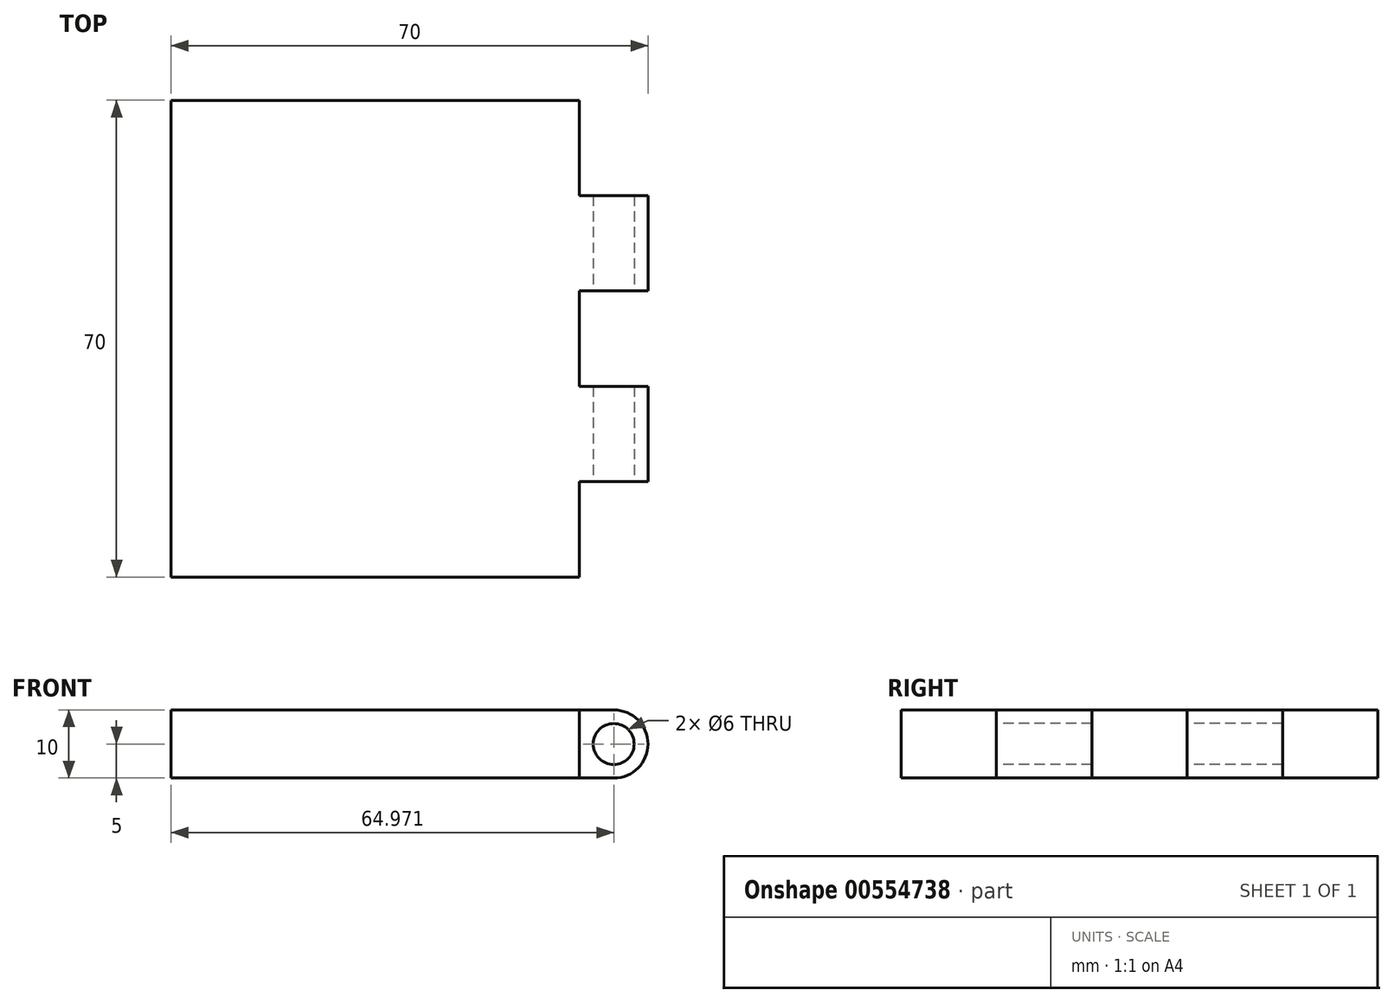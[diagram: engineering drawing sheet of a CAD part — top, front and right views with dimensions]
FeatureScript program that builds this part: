
annotation { "Feature Type Name" : "Feature", "Feature Type Description" : "" }
export const myFeature = defineFeature(function(context is Context, id is Id, definition is map)
    precondition{}
    {
        {
            var Q0;
            Q0=qCreatedBy(makeId("Top.planeOp"),FACE);
            var sketch = newSketch(context, id + "F0", { "sketchPlane" : qUnion([Q0])});
            skPoint(sketch, "E0.middle", {"position": v(0.02, 0.14) * mm});
            skLineSegment(sketch, "E1.0", {"start": v(24.97, 35.14) * mm, "end": v(-34.98, 35.14) * mm});
            skLineSegment(sketch, "E1.1", {"start": v(35.02, 21.14) * mm, "end": v(35.02, 7.14) * mm});
            skLineSegment(sketch, "E1.2", {"start": v(24.97, -34.86) * mm, "end": v(-34.98, -34.86) * mm});
            skLineSegment(sketch, "E1.3", {"start": v(-34.98, 35.14) * mm, "end": v(-34.98, -34.86) * mm});
            skLineSegment(sketch, "E2", {"start": v(25.02, -20.86) * mm, "end": v(35.02, -20.86) * mm});
            skLineSegment(sketch, "E3", {"start": v(25.02, -6.86) * mm, "end": v(35.02, -6.86) * mm});
            skLineSegment(sketch, "E4", {"start": v(25.02, 7.14) * mm, "end": v(35.02, 7.14) * mm});
            skLineSegment(sketch, "E5", {"start": v(25.02, 21.14) * mm, "end": v(35.02, 21.14) * mm});
            skPoint(sketch, "E6.orphan", {"position": v(25.02, -34.86) * mm});
            skLineSegment(sketch, "E7.trimOffspring", {"start": v(35.02, -6.86) * mm, "end": v(35.02, -20.86) * mm});
            skPoint(sketch, "E0.right.end.orphan", {"position": v(-24.98, -24.86) * mm});
            skPoint(sketch, "E0.bottom.end.orphan", {"position": v(-24.98, 25.14) * mm});
            skLineSegment(sketch, "E8", {"start": v(25.02, -20.86) * mm, "end": v(24.97, -20.86) * mm});
            skLineSegment(sketch, "E9", {"start": v(24.97, -20.86) * mm, "end": v(24.97, -34.86) * mm});
            skLineSegment(sketch, "E10", {"start": v(24.97, -6.86) * mm, "end": v(24.97, 35.14) * mm});
            skLineSegment(sketch, "E11", {"start": v(25.02, 21.14) * mm, "end": v(24.97, 21.14) * mm});
            skPoint(sketch, "E12.end.orphan", {"position": v(25.02, 35.14) * mm});
            skPoint(sketch, "E12.start.orphan", {"position": v(25.02, 25.14) * mm});
            skLineSegment(sketch, "E13", {"start": v(25.02, 7.14) * mm, "end": v(24.97, 7.14) * mm});
            skLineSegment(sketch, "E14", {"start": v(25.02, -6.86) * mm, "end": v(24.97, -6.86) * mm});
            skPoint(sketch, "E15.start.orphan", {"position": v(25.02, -24.86) * mm});
            skLineSegment(sketch, "E16.trimOffspring", {"start": v(25.02, -6.86) * mm, "end": v(25.02, -20.86) * mm});
            skSolve(sketch);
        }
        {
            var Q0;
            Q0=makeQuery(id+"F0.imprint","IMPRINT",FACE,{"disambiguationData":[TD([[makeQuery(id+"F0.imprint","IMPRINT",EDGE,{"derivedFrom":sQuery(id+"F0.wireOp",EDGE,"E0.bottom")}),-1.0]])]});
            var Q1;
            {var subQ3=sQuery(id+"F0.wireOp",EDGE,"E0.bottom");Q1=makeQuery(id+"F0.imprint","IMPRINT",FACE,{"disambiguationData":[TD([[makeQuery(id+"F0.imprint","IMPRINT",EDGE,{"derivedFrom":subQ3}),1.0]])]});}
            var Q2;
            {var subQ0=sQuery(id+"F0.wireOp",EDGE,"E2");Q2=makeQuery(id+"F0.imprint","IMPRINT",FACE,{"disambiguationData":[TD([[makeQuery(id+"F0.imprint","IMPRINT",EDGE,{"derivedFrom":subQ0}),1.0]])]});}
            var Q3;
            Q3=makeQuery(id+"F0.imprint","IMPRINT",FACE,{"disambiguationData":[TD([[makeQuery(id+"F0.imprint","IMPRINT",EDGE,{"derivedFrom":sQuery(id+"F0.wireOp",EDGE,"E1.1")}),-1.0]])]});
            var Q4;
            {var subQ1=sQuery(id+"F0.wireOp",EDGE,"E1.0");Q4=makeQuery(id+"F0.imprint","IMPRINT",FACE,{"disambiguationData":[TD([[makeQuery(id+"F0.imprint","IMPRINT",EDGE,{"derivedFrom":subQ1}),1.0]])]});}
            extrude(context, id + "F1", {"entities" : qUnion([Q0, Q1, Q2, Q3, Q4]), "depth" : 10 * mm, "offsetDistance" : 25 * mm});
        }
        {
            var Q0;
            Q0=makeQuery(id+"F1.opExtrude","SWEPT_FACE",FACE,{"disambiguationData":[OSD([sQuery(id+"F0.wireOp",EDGE,"E2")])]});
            var sketch = newSketch(context, id + "F2", { "sketchPlane" : qUnion([Q0])});
            skCircle(sketch, "E17", {"center": v(30, 5) * mm, "radius": 3 * mm});
            skPoint(sketch, "E17.centerSnap0", {"position": v(30, 10) * mm});
            skPoint(sketch, "E17.centerSnap1", {"position": v(35.02, 5) * mm});
            skArc(sketch, "E18", {"start": v(35.02, 5) * mm, "mid": v(33.54, 8.54) * mm, "end": v(30, 10) * mm});
            skArc(sketch, "E19", {"start": v(30, 0) * mm, "mid": v(33.54, 1.46) * mm, "end": v(35.02, 5) * mm});
            skSolve(sketch);
        }
        {
            var Q0;
            Q0=makeQuery(id+"F2.imprint","IMPRINT",FACE,{"disambiguationData":[TD([[makeQuery(id+"F2.imprint","IMPRINT",EDGE,{"derivedFrom":sQuery(id+"F2.wireOp",EDGE,"E17")}),1.0]])]});
            var Q1;
            {var subQ0=sQuery(id+"F2.wireOp",EDGE,"E18");Q1=makeQuery(id+"F2.imprint","IMPRINT",FACE,{"disambiguationData":[TD([[makeQuery(id+"F2.imprint","IMPRINT",EDGE,{"derivedFrom":subQ0}),-1.0]])]});}
            var Q2;
            {var subQ0=sQuery(id+"F2.wireOp",EDGE,"E19");Q2=makeQuery(id+"F2.imprint","IMPRINT",FACE,{"disambiguationData":[TD([[makeQuery(id+"F2.imprint","IMPRINT",EDGE,{"derivedFrom":subQ0}),-1.0]])]});}
            extrude(context, id + "F3", {"entities" : qUnion([Q0, Q1, Q2]), "operationType" : NewBodyOperationType.REMOVE, "endBound" : BoundingType.THROUGH_ALL, "oppositeDirection" : true, "depth" : 25 * mm, "offsetDistance" : 25 * mm});
        }
    });
